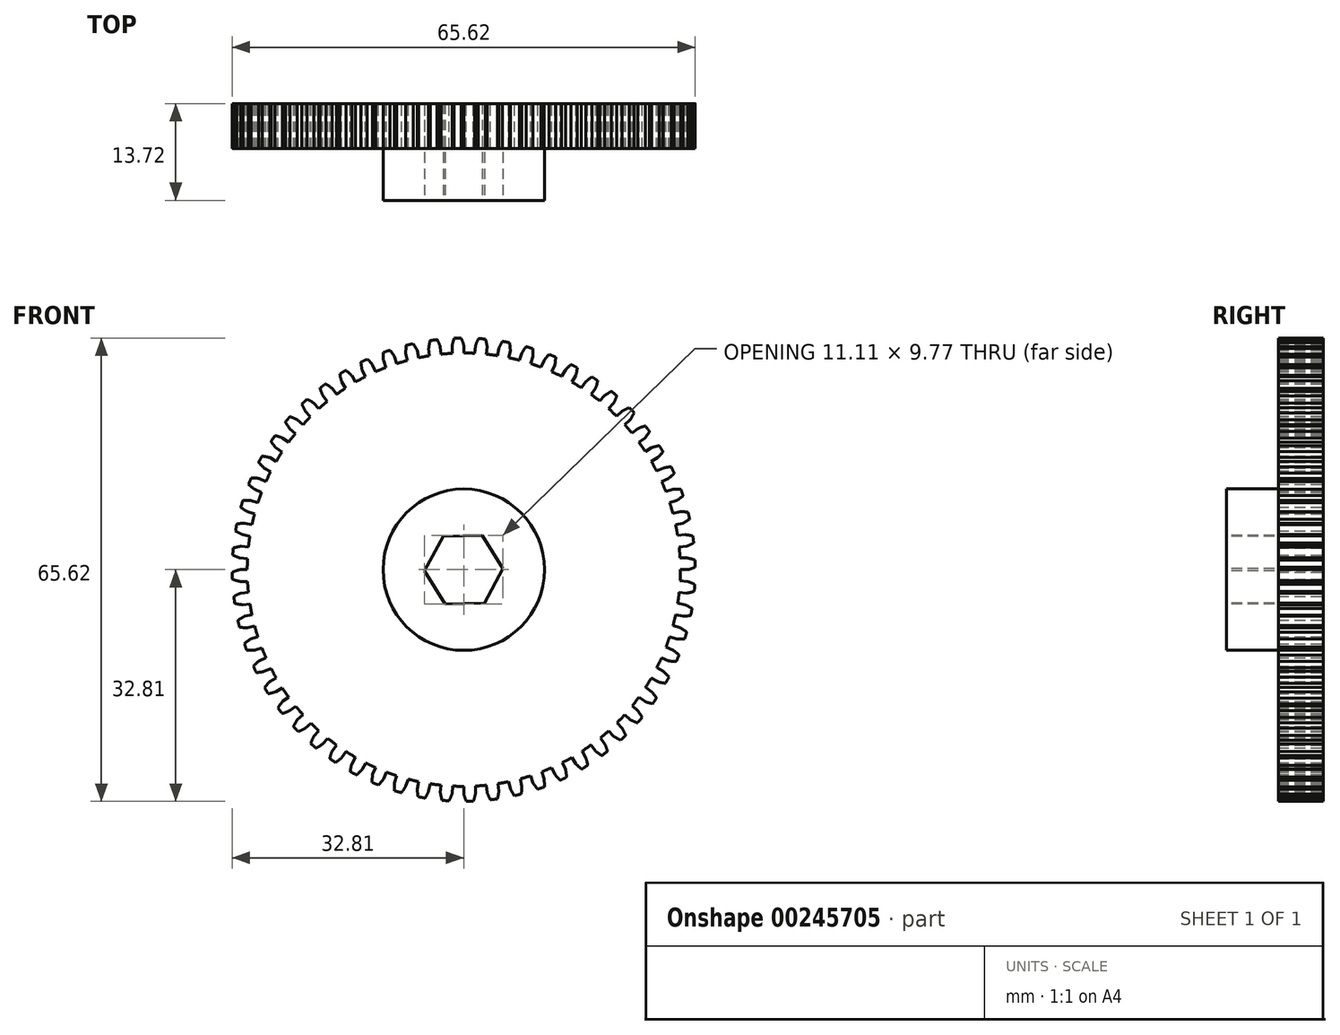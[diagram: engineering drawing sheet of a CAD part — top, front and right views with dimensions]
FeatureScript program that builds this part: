
annotation { "Feature Type Name" : "Feature", "Feature Type Description" : "" }
export const myFeature = defineFeature(function(context is Context, id is Id, definition is map)
    precondition{}
    {
        {
            var Q0;
            Q0=qCreatedBy(makeId("Front.planeOp"),FACE);
            var sketch = newSketch(context, id + "F0", { "sketchPlane" : qUnion([Q0])});
            skCircle(sketch, "E0", {"center": v(0, 0) * mm, "radius": 30.7 * mm});
            skArc(sketch, "E1", {"start": v(-0.36, 32.8) * mm, "mid": v(-0.6, 32.8) * mm, "end": v(-0.86, 32.8) * mm});
            skLineSegment(sketch, "E2", {"start": v(0, 30.7) * mm, "end": v(0, 31.75) * mm});
            skArc(sketch, "E3", {"start": v(-7.94, 31.83) * mm, "mid": v(-7.94, 31.8) * mm, "end": v(-7.94, 31.75) * mm});
            skArc(sketch, "E4.trimOffspring", {"start": v(0, 31.75) * mm, "mid": v(-0.16, 32.28) * mm, "end": v(-0.36, 32.8) * mm});
            skArc(sketch, "E5.trimOffspring", {"start": v(-7.94, 31.83) * mm, "mid": v(-8.1, 31.8) * mm, "end": v(-8.26, 31.75) * mm});
            skLineSegment(sketch, "E6.trimOffspring", {"start": v(-7.94, 31.75) * mm, "end": v(-8.26, 31.75) * mm});
            skArc(sketch, "E7.MirrorCS", {"start": v(-1.36, 32.78) * mm, "mid": v(-1.1, 32.79) * mm, "end": v(-0.86, 32.8) * mm});
            skArc(sketch, "E8.MirrorCS", {"start": v(-1.66, 31.7) * mm, "mid": v(-1.53, 32.25) * mm, "end": v(-1.36, 32.78) * mm});
            skLineSegment(sketch, "E9", {"start": v(-1.66, 31.7) * mm, "end": v(-1.66, 30.65) * mm});
            skArc(sketch, "E10.1.0", {"start": v(-3.32, 31.58) * mm, "mid": v(-3.54, 32.1) * mm, "end": v(-3.79, 32.59) * mm});
            skLineSegment(sketch, "E10.1.1", {"start": v(-3.2, 30.52) * mm, "end": v(-3.32, 31.58) * mm});
            skLineSegment(sketch, "E10.1.2", {"start": v(-4.97, 31.36) * mm, "end": v(-4.86, 30.3) * mm});
            skArc(sketch, "E10.1.3", {"start": v(-4.97, 31.36) * mm, "mid": v(-4.9, 31.91) * mm, "end": v(-4.78, 32.46) * mm});
            skArc(sketch, "E10.1.4", {"start": v(-4.78, 32.46) * mm, "mid": v(-4.53, 32.5) * mm, "end": v(-4.28, 32.53) * mm});
            skArc(sketch, "E10.1.5", {"start": v(-3.79, 32.59) * mm, "mid": v(-4.04, 32.56) * mm, "end": v(-4.28, 32.53) * mm});
            skArc(sketch, "E10.2.0", {"start": v(-6.6, 31.06) * mm, "mid": v(-6.87, 31.55) * mm, "end": v(-7.17, 32.01) * mm});
            skLineSegment(sketch, "E10.2.1", {"start": v(-6.38, 30.02) * mm, "end": v(-6.6, 31.06) * mm});
            skLineSegment(sketch, "E10.2.2", {"start": v(-8.22, 30.67) * mm, "end": v(-8, 29.63) * mm});
            skArc(sketch, "E10.2.3", {"start": v(-8.22, 30.67) * mm, "mid": v(-8.2, 31.23) * mm, "end": v(-8.14, 31.78) * mm});
            skArc(sketch, "E10.2.4", {"start": v(-8.14, 31.78) * mm, "mid": v(-7.9, 31.84) * mm, "end": v(-7.66, 31.9) * mm});
            skArc(sketch, "E10.2.5", {"start": v(-7.17, 32.01) * mm, "mid": v(-7.42, 31.96) * mm, "end": v(-7.66, 31.9) * mm});
            skArc(sketch, "E10.3.0", {"start": v(-9.81, 30.2) * mm, "mid": v(-10.13, 30.65) * mm, "end": v(-10.48, 31.09) * mm});
            skLineSegment(sketch, "E10.3.1", {"start": v(-9.48, 29.19) * mm, "end": v(-9.81, 30.2) * mm});
            skLineSegment(sketch, "E10.3.2", {"start": v(-11.38, 29.64) * mm, "end": v(-11.05, 28.63) * mm});
            skArc(sketch, "E10.3.3", {"start": v(-11.38, 29.64) * mm, "mid": v(-11.42, 30.2) * mm, "end": v(-11.42, 30.76) * mm});
            skArc(sketch, "E10.3.4", {"start": v(-11.42, 30.76) * mm, "mid": v(-11.19, 30.84) * mm, "end": v(-10.95, 30.93) * mm});
            skArc(sketch, "E10.3.5", {"start": v(-10.48, 31.09) * mm, "mid": v(-10.72, 31) * mm, "end": v(-10.95, 30.93) * mm});
            skArc(sketch, "E10.4.0", {"start": v(-12.91, 29) * mm, "mid": v(-13.28, 29.43) * mm, "end": v(-13.67, 29.82) * mm});
            skLineSegment(sketch, "E10.4.1", {"start": v(-12.48, 28.04) * mm, "end": v(-12.91, 29) * mm});
            skLineSegment(sketch, "E10.4.2", {"start": v(-14.41, 28.29) * mm, "end": v(-13.98, 27.32) * mm});
            skArc(sketch, "E10.4.3", {"start": v(-14.41, 28.29) * mm, "mid": v(-14.51, 28.84) * mm, "end": v(-14.57, 29.4) * mm});
            skArc(sketch, "E10.4.4", {"start": v(-14.57, 29.4) * mm, "mid": v(-14.35, 29.5) * mm, "end": v(-14.12, 29.61) * mm});
            skArc(sketch, "E10.4.5", {"start": v(-13.67, 29.82) * mm, "mid": v(-13.9, 29.72) * mm, "end": v(-14.12, 29.61) * mm});
            skArc(sketch, "E10.5.0", {"start": v(-15.88, 27.5) * mm, "mid": v(-16.28, 27.88) * mm, "end": v(-16.72, 28.23) * mm});
            skLineSegment(sketch, "E10.5.1", {"start": v(-15.35, 26.58) * mm, "end": v(-15.87, 27.5) * mm});
            skLineSegment(sketch, "E10.5.2", {"start": v(-17.3, 26.63) * mm, "end": v(-16.76, 25.7) * mm});
            skArc(sketch, "E10.5.3", {"start": v(-17.3, 26.63) * mm, "mid": v(-17.45, 27.16) * mm, "end": v(-17.56, 27.7) * mm});
            skArc(sketch, "E10.5.4", {"start": v(-17.56, 27.7) * mm, "mid": v(-17.35, 27.84) * mm, "end": v(-17.14, 27.97) * mm});
            skArc(sketch, "E10.5.5", {"start": v(-16.72, 28.23) * mm, "mid": v(-16.93, 28.1) * mm, "end": v(-17.14, 27.97) * mm});
            skArc(sketch, "E10.6.0", {"start": v(-18.66, 25.69) * mm, "mid": v(-19.1, 26.02) * mm, "end": v(-19.57, 26.33) * mm});
            skLineSegment(sketch, "E10.6.1", {"start": v(-18.04, 24.83) * mm, "end": v(-18.66, 25.69) * mm});
            skLineSegment(sketch, "E10.6.2", {"start": v(-19.98, 24.67) * mm, "end": v(-19.36, 23.82) * mm});
            skArc(sketch, "E10.6.3", {"start": v(-19.98, 24.67) * mm, "mid": v(-20.2, 25.2) * mm, "end": v(-20.36, 25.72) * mm});
            skArc(sketch, "E10.6.4", {"start": v(-20.36, 25.72) * mm, "mid": v(-20.17, 25.88) * mm, "end": v(-19.97, 26.03) * mm});
            skArc(sketch, "E10.6.5", {"start": v(-19.57, 26.33) * mm, "mid": v(-19.77, 26.18) * mm, "end": v(-19.97, 26.03) * mm});
            skArc(sketch, "E10.7.0", {"start": v(-21.24, 23.6) * mm, "mid": v(-21.72, 23.88) * mm, "end": v(-22.22, 24.14) * mm});
            skLineSegment(sketch, "E10.7.1", {"start": v(-20.54, 22.8) * mm, "end": v(-21.24, 23.6) * mm});
            skLineSegment(sketch, "E10.7.2", {"start": v(-22.45, 22.45) * mm, "end": v(-21.74, 21.66) * mm});
            skArc(sketch, "E10.7.3", {"start": v(-22.45, 22.45) * mm, "mid": v(-22.71, 22.94) * mm, "end": v(-22.94, 23.45) * mm});
            skArc(sketch, "E10.7.4", {"start": v(-22.94, 23.45) * mm, "mid": v(-22.76, 23.63) * mm, "end": v(-22.58, 23.8) * mm});
            skArc(sketch, "E10.7.5", {"start": v(-22.22, 24.14) * mm, "mid": v(-22.4, 23.97) * mm, "end": v(-22.58, 23.8) * mm});
            skArc(sketch, "E10.8.0", {"start": v(-23.6, 21.24) * mm, "mid": v(-24.1, 21.48) * mm, "end": v(-24.62, 21.68) * mm});
            skLineSegment(sketch, "E10.8.1", {"start": v(-22.8, 20.54) * mm, "end": v(-23.6, 21.24) * mm});
            skLineSegment(sketch, "E10.8.2", {"start": v(-24.67, 19.98) * mm, "end": v(-23.89, 19.27) * mm});
            skArc(sketch, "E10.8.3", {"start": v(-24.67, 19.98) * mm, "mid": v(-24.99, 20.44) * mm, "end": v(-25.27, 20.93) * mm});
            skArc(sketch, "E10.8.4", {"start": v(-25.27, 20.93) * mm, "mid": v(-25.1, 21.12) * mm, "end": v(-24.95, 21.3) * mm});
            skArc(sketch, "E10.8.5", {"start": v(-24.62, 21.68) * mm, "mid": v(-24.78, 21.5) * mm, "end": v(-24.95, 21.3) * mm});
            skArc(sketch, "E10.9.0", {"start": v(-25.69, 18.66) * mm, "mid": v(-26.21, 18.85) * mm, "end": v(-26.75, 19) * mm});
            skLineSegment(sketch, "E10.9.1", {"start": v(-24.83, 18.04) * mm, "end": v(-25.69, 18.66) * mm});
            skLineSegment(sketch, "E10.9.2", {"start": v(-26.63, 17.3) * mm, "end": v(-25.77, 16.67) * mm});
            skArc(sketch, "E10.9.3", {"start": v(-26.63, 17.3) * mm, "mid": v(-26.99, 17.72) * mm, "end": v(-27.32, 18.17) * mm});
            skArc(sketch, "E10.9.4", {"start": v(-27.32, 18.17) * mm, "mid": v(-27.18, 18.38) * mm, "end": v(-27.04, 18.58) * mm});
            skArc(sketch, "E10.9.5", {"start": v(-26.75, 19) * mm, "mid": v(-26.9, 18.79) * mm, "end": v(-27.04, 18.58) * mm});
            skArc(sketch, "E10.10.0", {"start": v(-27.5, 15.88) * mm, "mid": v(-28.04, 16) * mm, "end": v(-28.6, 16.1) * mm});
            skLineSegment(sketch, "E10.10.1", {"start": v(-26.58, 15.35) * mm, "end": v(-27.5, 15.88) * mm});
            skLineSegment(sketch, "E10.10.2", {"start": v(-28.29, 14.41) * mm, "end": v(-27.37, 13.88) * mm});
            skArc(sketch, "E10.10.3", {"start": v(-28.29, 14.41) * mm, "mid": v(-28.7, 14.8) * mm, "end": v(-29.07, 15.22) * mm});
            skArc(sketch, "E10.10.4", {"start": v(-29.07, 15.22) * mm, "mid": v(-28.95, 15.44) * mm, "end": v(-28.83, 15.65) * mm});
            skArc(sketch, "E10.10.5", {"start": v(-28.6, 16.1) * mm, "mid": v(-28.71, 15.87) * mm, "end": v(-28.83, 15.65) * mm});
            skArc(sketch, "E10.11.0", {"start": v(-29, 12.91) * mm, "mid": v(-29.56, 12.98) * mm, "end": v(-30.12, 13.01) * mm});
            skLineSegment(sketch, "E10.11.1", {"start": v(-28.04, 12.48) * mm, "end": v(-29, 12.91) * mm});
            skLineSegment(sketch, "E10.11.2", {"start": v(-29.64, 11.38) * mm, "end": v(-28.67, 10.95) * mm});
            skArc(sketch, "E10.11.3", {"start": v(-29.64, 11.38) * mm, "mid": v(-30.08, 11.72) * mm, "end": v(-30.5, 12.1) * mm});
            skArc(sketch, "E10.11.4", {"start": v(-30.5, 12.1) * mm, "mid": v(-30.4, 12.32) * mm, "end": v(-30.31, 12.56) * mm});
            skArc(sketch, "E10.11.5", {"start": v(-30.12, 13.01) * mm, "mid": v(-30.21, 12.78) * mm, "end": v(-30.31, 12.56) * mm});
            skArc(sketch, "E10.12.0", {"start": v(-30.2, 9.81) * mm, "mid": v(-30.75, 9.82) * mm, "end": v(-31.31, 9.8) * mm});
            skLineSegment(sketch, "E10.12.1", {"start": v(-29.19, 9.48) * mm, "end": v(-30.2, 9.81) * mm});
            skLineSegment(sketch, "E10.12.2", {"start": v(-30.67, 8.22) * mm, "end": v(-29.66, 7.89) * mm});
            skArc(sketch, "E10.12.3", {"start": v(-30.67, 8.22) * mm, "mid": v(-31.14, 8.51) * mm, "end": v(-31.6, 8.84) * mm});
            skArc(sketch, "E10.12.4", {"start": v(-31.6, 8.84) * mm, "mid": v(-31.53, 9.08) * mm, "end": v(-31.46, 9.32) * mm});
            skArc(sketch, "E10.12.5", {"start": v(-31.31, 9.8) * mm, "mid": v(-31.39, 9.56) * mm, "end": v(-31.46, 9.32) * mm});
            skArc(sketch, "E10.13.0", {"start": v(-31.06, 6.6) * mm, "mid": v(-31.61, 6.55) * mm, "end": v(-32.16, 6.47) * mm});
            skLineSegment(sketch, "E10.13.1", {"start": v(-30.02, 6.38) * mm, "end": v(-31.06, 6.6) * mm});
            skLineSegment(sketch, "E10.13.2", {"start": v(-31.36, 4.97) * mm, "end": v(-30.32, 4.75) * mm});
            skArc(sketch, "E10.13.3", {"start": v(-31.36, 4.97) * mm, "mid": v(-31.86, 5.21) * mm, "end": v(-32.35, 5.49) * mm});
            skArc(sketch, "E10.13.4", {"start": v(-32.35, 5.49) * mm, "mid": v(-32.3, 5.73) * mm, "end": v(-32.26, 5.98) * mm});
            skArc(sketch, "E10.13.5", {"start": v(-32.16, 6.47) * mm, "mid": v(-32.21, 6.22) * mm, "end": v(-32.26, 5.98) * mm});
            skArc(sketch, "E10.14.0", {"start": v(-31.58, 3.32) * mm, "mid": v(-32.12, 3.21) * mm, "end": v(-32.66, 3.07) * mm});
            skLineSegment(sketch, "E10.14.1", {"start": v(-30.52, 3.2) * mm, "end": v(-31.58, 3.32) * mm});
            skLineSegment(sketch, "E10.14.2", {"start": v(-31.7, 1.66) * mm, "end": v(-30.65, 1.55) * mm});
            skArc(sketch, "E10.14.3", {"start": v(-31.7, 1.66) * mm, "mid": v(-32.23, 1.85) * mm, "end": v(-32.74, 2.08) * mm});
            skArc(sketch, "E10.14.4", {"start": v(-32.74, 2.08) * mm, "mid": v(-32.73, 2.33) * mm, "end": v(-32.7, 2.57) * mm});
            skArc(sketch, "E10.14.5", {"start": v(-32.66, 3.07) * mm, "mid": v(-32.69, 2.82) * mm, "end": v(-32.7, 2.57) * mm});
            skArc(sketch, "E10.15.0", {"start": v(-31.75, 0) * mm, "mid": v(-32.28, -0.16) * mm, "end": v(-32.8, -0.36) * mm});
            skLineSegment(sketch, "E10.15.1", {"start": v(-30.7, 0) * mm, "end": v(-31.75, 0) * mm});
            skLineSegment(sketch, "E10.15.2", {"start": v(-31.7, -1.66) * mm, "end": v(-30.65, -1.66) * mm});
            skArc(sketch, "E10.15.3", {"start": v(-31.7, -1.66) * mm, "mid": v(-32.25, -1.53) * mm, "end": v(-32.78, -1.36) * mm});
            skArc(sketch, "E10.15.4", {"start": v(-32.78, -1.36) * mm, "mid": v(-32.79, -1.1) * mm, "end": v(-32.8, -0.86) * mm});
            skArc(sketch, "E10.15.5", {"start": v(-32.8, -0.36) * mm, "mid": v(-32.8, -0.6) * mm, "end": v(-32.8, -0.86) * mm});
            skArc(sketch, "E10.16.0", {"start": v(-31.58, -3.32) * mm, "mid": v(-32.1, -3.54) * mm, "end": v(-32.59, -3.79) * mm});
            skLineSegment(sketch, "E10.16.1", {"start": v(-30.52, -3.2) * mm, "end": v(-31.58, -3.32) * mm});
            skLineSegment(sketch, "E10.16.2", {"start": v(-31.36, -4.97) * mm, "end": v(-30.3, -4.86) * mm});
            skArc(sketch, "E10.16.3", {"start": v(-31.36, -4.97) * mm, "mid": v(-31.91, -4.9) * mm, "end": v(-32.46, -4.78) * mm});
            skArc(sketch, "E10.16.4", {"start": v(-32.46, -4.78) * mm, "mid": v(-32.5, -4.53) * mm, "end": v(-32.53, -4.28) * mm});
            skArc(sketch, "E10.16.5", {"start": v(-32.59, -3.79) * mm, "mid": v(-32.56, -4.04) * mm, "end": v(-32.53, -4.28) * mm});
            skArc(sketch, "E10.17.0", {"start": v(-31.06, -6.6) * mm, "mid": v(-31.55, -6.87) * mm, "end": v(-32.01, -7.17) * mm});
            skLineSegment(sketch, "E10.17.1", {"start": v(-30.02, -6.38) * mm, "end": v(-31.06, -6.6) * mm});
            skLineSegment(sketch, "E10.17.2", {"start": v(-30.67, -8.22) * mm, "end": v(-29.63, -8) * mm});
            skArc(sketch, "E10.17.3", {"start": v(-30.67, -8.22) * mm, "mid": v(-31.23, -8.2) * mm, "end": v(-31.78, -8.14) * mm});
            skArc(sketch, "E10.17.4", {"start": v(-31.78, -8.14) * mm, "mid": v(-31.84, -7.9) * mm, "end": v(-31.9, -7.66) * mm});
            skArc(sketch, "E10.17.5", {"start": v(-32.01, -7.17) * mm, "mid": v(-31.96, -7.42) * mm, "end": v(-31.9, -7.66) * mm});
            skArc(sketch, "E10.18.0", {"start": v(-30.2, -9.81) * mm, "mid": v(-30.65, -10.13) * mm, "end": v(-31.09, -10.48) * mm});
            skLineSegment(sketch, "E10.18.1", {"start": v(-29.19, -9.48) * mm, "end": v(-30.2, -9.81) * mm});
            skLineSegment(sketch, "E10.18.2", {"start": v(-29.64, -11.38) * mm, "end": v(-28.63, -11.05) * mm});
            skArc(sketch, "E10.18.3", {"start": v(-29.64, -11.38) * mm, "mid": v(-30.2, -11.42) * mm, "end": v(-30.76, -11.42) * mm});
            skArc(sketch, "E10.18.4", {"start": v(-30.76, -11.42) * mm, "mid": v(-30.84, -11.19) * mm, "end": v(-30.93, -10.95) * mm});
            skArc(sketch, "E10.18.5", {"start": v(-31.09, -10.48) * mm, "mid": v(-31, -10.72) * mm, "end": v(-30.93, -10.95) * mm});
            skArc(sketch, "E10.19.0", {"start": v(-29, -12.91) * mm, "mid": v(-29.43, -13.28) * mm, "end": v(-29.82, -13.67) * mm});
            skLineSegment(sketch, "E10.19.1", {"start": v(-28.04, -12.48) * mm, "end": v(-29, -12.91) * mm});
            skLineSegment(sketch, "E10.19.2", {"start": v(-28.29, -14.41) * mm, "end": v(-27.32, -13.98) * mm});
            skArc(sketch, "E10.19.3", {"start": v(-28.29, -14.41) * mm, "mid": v(-28.84, -14.51) * mm, "end": v(-29.4, -14.57) * mm});
            skArc(sketch, "E10.19.4", {"start": v(-29.4, -14.57) * mm, "mid": v(-29.5, -14.35) * mm, "end": v(-29.61, -14.12) * mm});
            skArc(sketch, "E10.19.5", {"start": v(-29.82, -13.67) * mm, "mid": v(-29.72, -13.9) * mm, "end": v(-29.61, -14.12) * mm});
            skArc(sketch, "E10.20.0", {"start": v(-27.5, -15.87) * mm, "mid": v(-27.88, -16.28) * mm, "end": v(-28.23, -16.72) * mm});
            skLineSegment(sketch, "E10.20.1", {"start": v(-26.58, -15.35) * mm, "end": v(-27.5, -15.87) * mm});
            skLineSegment(sketch, "E10.20.2", {"start": v(-26.63, -17.3) * mm, "end": v(-25.7, -16.76) * mm});
            skArc(sketch, "E10.20.3", {"start": v(-26.63, -17.3) * mm, "mid": v(-27.16, -17.45) * mm, "end": v(-27.7, -17.56) * mm});
            skArc(sketch, "E10.20.4", {"start": v(-27.7, -17.56) * mm, "mid": v(-27.84, -17.35) * mm, "end": v(-27.97, -17.14) * mm});
            skArc(sketch, "E10.20.5", {"start": v(-28.23, -16.72) * mm, "mid": v(-28.1, -16.93) * mm, "end": v(-27.97, -17.14) * mm});
            skArc(sketch, "E10.21.0", {"start": v(-25.69, -18.66) * mm, "mid": v(-26.02, -19.1) * mm, "end": v(-26.33, -19.57) * mm});
            skLineSegment(sketch, "E10.21.1", {"start": v(-24.83, -18.04) * mm, "end": v(-25.69, -18.66) * mm});
            skLineSegment(sketch, "E10.21.2", {"start": v(-24.67, -19.98) * mm, "end": v(-23.82, -19.36) * mm});
            skArc(sketch, "E10.21.3", {"start": v(-24.67, -19.98) * mm, "mid": v(-25.2, -20.2) * mm, "end": v(-25.72, -20.36) * mm});
            skArc(sketch, "E10.21.4", {"start": v(-25.72, -20.36) * mm, "mid": v(-25.88, -20.17) * mm, "end": v(-26.03, -19.97) * mm});
            skArc(sketch, "E10.21.5", {"start": v(-26.33, -19.57) * mm, "mid": v(-26.18, -19.77) * mm, "end": v(-26.03, -19.97) * mm});
            skArc(sketch, "E10.22.0", {"start": v(-23.6, -21.24) * mm, "mid": v(-23.88, -21.72) * mm, "end": v(-24.14, -22.22) * mm});
            skLineSegment(sketch, "E10.22.1", {"start": v(-22.8, -20.54) * mm, "end": v(-23.6, -21.24) * mm});
            skLineSegment(sketch, "E10.22.2", {"start": v(-22.45, -22.45) * mm, "end": v(-21.66, -21.74) * mm});
            skArc(sketch, "E10.22.3", {"start": v(-22.45, -22.45) * mm, "mid": v(-22.94, -22.71) * mm, "end": v(-23.45, -22.94) * mm});
            skArc(sketch, "E10.22.4", {"start": v(-23.45, -22.94) * mm, "mid": v(-23.63, -22.76) * mm, "end": v(-23.8, -22.58) * mm});
            skArc(sketch, "E10.22.5", {"start": v(-24.14, -22.22) * mm, "mid": v(-23.97, -22.4) * mm, "end": v(-23.8, -22.58) * mm});
            skArc(sketch, "E10.23.0", {"start": v(-21.24, -23.6) * mm, "mid": v(-21.48, -24.1) * mm, "end": v(-21.68, -24.62) * mm});
            skLineSegment(sketch, "E10.23.1", {"start": v(-20.54, -22.8) * mm, "end": v(-21.24, -23.6) * mm});
            skLineSegment(sketch, "E10.23.2", {"start": v(-19.98, -24.67) * mm, "end": v(-19.27, -23.89) * mm});
            skArc(sketch, "E10.23.3", {"start": v(-19.98, -24.67) * mm, "mid": v(-20.44, -24.99) * mm, "end": v(-20.93, -25.27) * mm});
            skArc(sketch, "E10.23.4", {"start": v(-20.93, -25.27) * mm, "mid": v(-21.12, -25.1) * mm, "end": v(-21.3, -24.95) * mm});
            skArc(sketch, "E10.23.5", {"start": v(-21.68, -24.62) * mm, "mid": v(-21.5, -24.78) * mm, "end": v(-21.3, -24.95) * mm});
            skArc(sketch, "E10.24.0", {"start": v(-18.66, -25.69) * mm, "mid": v(-18.85, -26.21) * mm, "end": v(-19, -26.75) * mm});
            skLineSegment(sketch, "E10.24.1", {"start": v(-18.04, -24.83) * mm, "end": v(-18.66, -25.69) * mm});
            skLineSegment(sketch, "E10.24.2", {"start": v(-17.3, -26.63) * mm, "end": v(-16.67, -25.77) * mm});
            skArc(sketch, "E10.24.3", {"start": v(-17.3, -26.63) * mm, "mid": v(-17.72, -26.99) * mm, "end": v(-18.17, -27.32) * mm});
            skArc(sketch, "E10.24.4", {"start": v(-18.17, -27.32) * mm, "mid": v(-18.38, -27.18) * mm, "end": v(-18.58, -27.04) * mm});
            skArc(sketch, "E10.24.5", {"start": v(-19, -26.75) * mm, "mid": v(-18.79, -26.9) * mm, "end": v(-18.58, -27.04) * mm});
            skArc(sketch, "E10.25.0", {"start": v(-15.87, -27.5) * mm, "mid": v(-16, -28.04) * mm, "end": v(-16.1, -28.6) * mm});
            skLineSegment(sketch, "E10.25.1", {"start": v(-15.35, -26.58) * mm, "end": v(-15.87, -27.5) * mm});
            skLineSegment(sketch, "E10.25.2", {"start": v(-14.41, -28.29) * mm, "end": v(-13.88, -27.37) * mm});
            skArc(sketch, "E10.25.3", {"start": v(-14.41, -28.29) * mm, "mid": v(-14.8, -28.7) * mm, "end": v(-15.22, -29.07) * mm});
            skArc(sketch, "E10.25.4", {"start": v(-15.22, -29.07) * mm, "mid": v(-15.44, -28.95) * mm, "end": v(-15.65, -28.83) * mm});
            skArc(sketch, "E10.25.5", {"start": v(-16.1, -28.6) * mm, "mid": v(-15.87, -28.71) * mm, "end": v(-15.65, -28.83) * mm});
            skArc(sketch, "E10.26.0", {"start": v(-12.91, -29) * mm, "mid": v(-12.98, -29.56) * mm, "end": v(-13.01, -30.12) * mm});
            skLineSegment(sketch, "E10.26.1", {"start": v(-12.48, -28.04) * mm, "end": v(-12.91, -29) * mm});
            skLineSegment(sketch, "E10.26.2", {"start": v(-11.38, -29.64) * mm, "end": v(-10.95, -28.67) * mm});
            skArc(sketch, "E10.26.3", {"start": v(-11.38, -29.64) * mm, "mid": v(-11.72, -30.08) * mm, "end": v(-12.1, -30.5) * mm});
            skArc(sketch, "E10.26.4", {"start": v(-12.1, -30.5) * mm, "mid": v(-12.32, -30.4) * mm, "end": v(-12.56, -30.31) * mm});
            skArc(sketch, "E10.26.5", {"start": v(-13.01, -30.12) * mm, "mid": v(-12.78, -30.21) * mm, "end": v(-12.56, -30.31) * mm});
            skArc(sketch, "E10.27.0", {"start": v(-9.81, -30.2) * mm, "mid": v(-9.82, -30.75) * mm, "end": v(-9.8, -31.31) * mm});
            skLineSegment(sketch, "E10.27.1", {"start": v(-9.48, -29.19) * mm, "end": v(-9.81, -30.2) * mm});
            skLineSegment(sketch, "E10.27.2", {"start": v(-8.22, -30.67) * mm, "end": v(-7.89, -29.66) * mm});
            skArc(sketch, "E10.27.3", {"start": v(-8.22, -30.67) * mm, "mid": v(-8.51, -31.14) * mm, "end": v(-8.84, -31.6) * mm});
            skArc(sketch, "E10.27.4", {"start": v(-8.84, -31.6) * mm, "mid": v(-9.08, -31.53) * mm, "end": v(-9.32, -31.46) * mm});
            skArc(sketch, "E10.27.5", {"start": v(-9.8, -31.31) * mm, "mid": v(-9.56, -31.39) * mm, "end": v(-9.32, -31.46) * mm});
            skArc(sketch, "E10.28.0", {"start": v(-6.6, -31.06) * mm, "mid": v(-6.55, -31.61) * mm, "end": v(-6.47, -32.16) * mm});
            skLineSegment(sketch, "E10.28.1", {"start": v(-6.38, -30.02) * mm, "end": v(-6.6, -31.06) * mm});
            skLineSegment(sketch, "E10.28.2", {"start": v(-4.97, -31.36) * mm, "end": v(-4.75, -30.32) * mm});
            skArc(sketch, "E10.28.3", {"start": v(-4.97, -31.36) * mm, "mid": v(-5.21, -31.86) * mm, "end": v(-5.49, -32.35) * mm});
            skArc(sketch, "E10.28.4", {"start": v(-5.49, -32.35) * mm, "mid": v(-5.73, -32.3) * mm, "end": v(-5.98, -32.26) * mm});
            skArc(sketch, "E10.28.5", {"start": v(-6.47, -32.16) * mm, "mid": v(-6.22, -32.21) * mm, "end": v(-5.98, -32.26) * mm});
            skArc(sketch, "E10.29.0", {"start": v(-3.32, -31.58) * mm, "mid": v(-3.21, -32.12) * mm, "end": v(-3.07, -32.66) * mm});
            skLineSegment(sketch, "E10.29.1", {"start": v(-3.2, -30.52) * mm, "end": v(-3.32, -31.58) * mm});
            skLineSegment(sketch, "E10.29.2", {"start": v(-1.66, -31.7) * mm, "end": v(-1.55, -30.65) * mm});
            skArc(sketch, "E10.29.3", {"start": v(-1.66, -31.7) * mm, "mid": v(-1.85, -32.23) * mm, "end": v(-2.08, -32.74) * mm});
            skArc(sketch, "E10.29.4", {"start": v(-2.08, -32.74) * mm, "mid": v(-2.33, -32.73) * mm, "end": v(-2.57, -32.7) * mm});
            skArc(sketch, "E10.29.5", {"start": v(-3.07, -32.66) * mm, "mid": v(-2.82, -32.69) * mm, "end": v(-2.57, -32.7) * mm});
            skArc(sketch, "E10.30.0", {"start": v(0, -31.75) * mm, "mid": v(0.16, -32.28) * mm, "end": v(0.36, -32.8) * mm});
            skLineSegment(sketch, "E10.30.1", {"start": v(0, -30.7) * mm, "end": v(0, -31.75) * mm});
            skLineSegment(sketch, "E10.30.2", {"start": v(1.66, -31.7) * mm, "end": v(1.66, -30.65) * mm});
            skArc(sketch, "E10.30.3", {"start": v(1.66, -31.7) * mm, "mid": v(1.53, -32.25) * mm, "end": v(1.36, -32.78) * mm});
            skArc(sketch, "E10.30.4", {"start": v(1.36, -32.78) * mm, "mid": v(1.1, -32.79) * mm, "end": v(0.86, -32.8) * mm});
            skArc(sketch, "E10.30.5", {"start": v(0.36, -32.8) * mm, "mid": v(0.6, -32.8) * mm, "end": v(0.86, -32.8) * mm});
            skArc(sketch, "E10.31.0", {"start": v(3.32, -31.58) * mm, "mid": v(3.54, -32.1) * mm, "end": v(3.79, -32.59) * mm});
            skLineSegment(sketch, "E10.31.1", {"start": v(3.2, -30.52) * mm, "end": v(3.32, -31.58) * mm});
            skLineSegment(sketch, "E10.31.2", {"start": v(4.97, -31.36) * mm, "end": v(4.86, -30.3) * mm});
            skArc(sketch, "E10.31.3", {"start": v(4.97, -31.36) * mm, "mid": v(4.9, -31.91) * mm, "end": v(4.78, -32.46) * mm});
            skArc(sketch, "E10.31.4", {"start": v(4.78, -32.46) * mm, "mid": v(4.53, -32.5) * mm, "end": v(4.28, -32.53) * mm});
            skArc(sketch, "E10.31.5", {"start": v(3.79, -32.59) * mm, "mid": v(4.04, -32.56) * mm, "end": v(4.28, -32.53) * mm});
            skArc(sketch, "E10.32.0", {"start": v(6.6, -31.06) * mm, "mid": v(6.87, -31.55) * mm, "end": v(7.17, -32.01) * mm});
            skLineSegment(sketch, "E10.32.1", {"start": v(6.38, -30.02) * mm, "end": v(6.6, -31.06) * mm});
            skLineSegment(sketch, "E10.32.2", {"start": v(8.22, -30.67) * mm, "end": v(8, -29.63) * mm});
            skArc(sketch, "E10.32.3", {"start": v(8.22, -30.67) * mm, "mid": v(8.2, -31.23) * mm, "end": v(8.14, -31.78) * mm});
            skArc(sketch, "E10.32.4", {"start": v(8.14, -31.78) * mm, "mid": v(7.9, -31.84) * mm, "end": v(7.66, -31.9) * mm});
            skArc(sketch, "E10.32.5", {"start": v(7.17, -32.01) * mm, "mid": v(7.42, -31.96) * mm, "end": v(7.66, -31.9) * mm});
            skArc(sketch, "E10.33.0", {"start": v(9.81, -30.2) * mm, "mid": v(10.13, -30.65) * mm, "end": v(10.48, -31.09) * mm});
            skLineSegment(sketch, "E10.33.1", {"start": v(9.48, -29.19) * mm, "end": v(9.81, -30.2) * mm});
            skLineSegment(sketch, "E10.33.2", {"start": v(11.38, -29.64) * mm, "end": v(11.05, -28.63) * mm});
            skArc(sketch, "E10.33.3", {"start": v(11.38, -29.64) * mm, "mid": v(11.42, -30.2) * mm, "end": v(11.42, -30.76) * mm});
            skArc(sketch, "E10.33.4", {"start": v(11.42, -30.76) * mm, "mid": v(11.19, -30.84) * mm, "end": v(10.95, -30.93) * mm});
            skArc(sketch, "E10.33.5", {"start": v(10.48, -31.09) * mm, "mid": v(10.72, -31) * mm, "end": v(10.95, -30.93) * mm});
            skArc(sketch, "E10.34.0", {"start": v(12.91, -29) * mm, "mid": v(13.28, -29.43) * mm, "end": v(13.67, -29.82) * mm});
            skLineSegment(sketch, "E10.34.1", {"start": v(12.48, -28.04) * mm, "end": v(12.91, -29) * mm});
            skLineSegment(sketch, "E10.34.2", {"start": v(14.41, -28.29) * mm, "end": v(13.98, -27.32) * mm});
            skArc(sketch, "E10.34.3", {"start": v(14.41, -28.29) * mm, "mid": v(14.51, -28.84) * mm, "end": v(14.57, -29.4) * mm});
            skArc(sketch, "E10.34.4", {"start": v(14.57, -29.4) * mm, "mid": v(14.35, -29.5) * mm, "end": v(14.12, -29.61) * mm});
            skArc(sketch, "E10.34.5", {"start": v(13.67, -29.82) * mm, "mid": v(13.9, -29.72) * mm, "end": v(14.12, -29.61) * mm});
            skArc(sketch, "E10.35.0", {"start": v(15.87, -27.5) * mm, "mid": v(16.28, -27.88) * mm, "end": v(16.72, -28.23) * mm});
            skLineSegment(sketch, "E10.35.1", {"start": v(15.35, -26.58) * mm, "end": v(15.87, -27.5) * mm});
            skLineSegment(sketch, "E10.35.2", {"start": v(17.3, -26.63) * mm, "end": v(16.76, -25.7) * mm});
            skArc(sketch, "E10.35.3", {"start": v(17.3, -26.63) * mm, "mid": v(17.45, -27.16) * mm, "end": v(17.56, -27.7) * mm});
            skArc(sketch, "E10.35.4", {"start": v(17.56, -27.7) * mm, "mid": v(17.35, -27.84) * mm, "end": v(17.14, -27.97) * mm});
            skArc(sketch, "E10.35.5", {"start": v(16.72, -28.23) * mm, "mid": v(16.93, -28.1) * mm, "end": v(17.14, -27.97) * mm});
            skArc(sketch, "E10.36.0", {"start": v(18.66, -25.69) * mm, "mid": v(19.1, -26.02) * mm, "end": v(19.57, -26.33) * mm});
            skLineSegment(sketch, "E10.36.1", {"start": v(18.04, -24.83) * mm, "end": v(18.66, -25.69) * mm});
            skLineSegment(sketch, "E10.36.2", {"start": v(19.98, -24.67) * mm, "end": v(19.36, -23.82) * mm});
            skArc(sketch, "E10.36.3", {"start": v(19.98, -24.67) * mm, "mid": v(20.2, -25.2) * mm, "end": v(20.36, -25.72) * mm});
            skArc(sketch, "E10.36.4", {"start": v(20.36, -25.72) * mm, "mid": v(20.17, -25.88) * mm, "end": v(19.97, -26.03) * mm});
            skArc(sketch, "E10.36.5", {"start": v(19.57, -26.33) * mm, "mid": v(19.77, -26.18) * mm, "end": v(19.97, -26.03) * mm});
            skArc(sketch, "E10.37.0", {"start": v(21.24, -23.6) * mm, "mid": v(21.72, -23.88) * mm, "end": v(22.22, -24.14) * mm});
            skLineSegment(sketch, "E10.37.1", {"start": v(20.54, -22.8) * mm, "end": v(21.24, -23.6) * mm});
            skLineSegment(sketch, "E10.37.2", {"start": v(22.45, -22.45) * mm, "end": v(21.74, -21.66) * mm});
            skArc(sketch, "E10.37.3", {"start": v(22.45, -22.45) * mm, "mid": v(22.71, -22.94) * mm, "end": v(22.94, -23.45) * mm});
            skArc(sketch, "E10.37.4", {"start": v(22.94, -23.45) * mm, "mid": v(22.76, -23.63) * mm, "end": v(22.58, -23.8) * mm});
            skArc(sketch, "E10.37.5", {"start": v(22.22, -24.14) * mm, "mid": v(22.4, -23.97) * mm, "end": v(22.58, -23.8) * mm});
            skArc(sketch, "E10.38.0", {"start": v(23.6, -21.24) * mm, "mid": v(24.1, -21.48) * mm, "end": v(24.62, -21.68) * mm});
            skLineSegment(sketch, "E10.38.1", {"start": v(22.8, -20.54) * mm, "end": v(23.6, -21.24) * mm});
            skLineSegment(sketch, "E10.38.2", {"start": v(24.67, -19.98) * mm, "end": v(23.89, -19.27) * mm});
            skArc(sketch, "E10.38.3", {"start": v(24.67, -19.98) * mm, "mid": v(24.99, -20.44) * mm, "end": v(25.27, -20.93) * mm});
            skArc(sketch, "E10.38.4", {"start": v(25.27, -20.93) * mm, "mid": v(25.1, -21.12) * mm, "end": v(24.95, -21.3) * mm});
            skArc(sketch, "E10.38.5", {"start": v(24.62, -21.68) * mm, "mid": v(24.78, -21.5) * mm, "end": v(24.95, -21.3) * mm});
            skArc(sketch, "E10.39.0", {"start": v(25.69, -18.66) * mm, "mid": v(26.21, -18.85) * mm, "end": v(26.75, -19) * mm});
            skLineSegment(sketch, "E10.39.1", {"start": v(24.83, -18.04) * mm, "end": v(25.69, -18.66) * mm});
            skLineSegment(sketch, "E10.39.2", {"start": v(26.63, -17.3) * mm, "end": v(25.77, -16.67) * mm});
            skArc(sketch, "E10.39.3", {"start": v(26.63, -17.3) * mm, "mid": v(26.99, -17.72) * mm, "end": v(27.32, -18.17) * mm});
            skArc(sketch, "E10.39.4", {"start": v(27.32, -18.17) * mm, "mid": v(27.18, -18.38) * mm, "end": v(27.04, -18.58) * mm});
            skArc(sketch, "E10.39.5", {"start": v(26.75, -19) * mm, "mid": v(26.9, -18.79) * mm, "end": v(27.04, -18.58) * mm});
            skArc(sketch, "E10.40.0", {"start": v(27.5, -15.88) * mm, "mid": v(28.04, -16) * mm, "end": v(28.6, -16.1) * mm});
            skLineSegment(sketch, "E10.40.1", {"start": v(26.58, -15.35) * mm, "end": v(27.5, -15.88) * mm});
            skLineSegment(sketch, "E10.40.2", {"start": v(28.29, -14.41) * mm, "end": v(27.37, -13.88) * mm});
            skArc(sketch, "E10.40.3", {"start": v(28.29, -14.41) * mm, "mid": v(28.7, -14.8) * mm, "end": v(29.07, -15.22) * mm});
            skArc(sketch, "E10.40.4", {"start": v(29.07, -15.22) * mm, "mid": v(28.95, -15.44) * mm, "end": v(28.83, -15.65) * mm});
            skArc(sketch, "E10.40.5", {"start": v(28.6, -16.1) * mm, "mid": v(28.71, -15.87) * mm, "end": v(28.83, -15.65) * mm});
            skArc(sketch, "E10.41.0", {"start": v(29, -12.91) * mm, "mid": v(29.56, -12.98) * mm, "end": v(30.12, -13.01) * mm});
            skLineSegment(sketch, "E10.41.1", {"start": v(28.04, -12.48) * mm, "end": v(29, -12.91) * mm});
            skLineSegment(sketch, "E10.41.2", {"start": v(29.64, -11.38) * mm, "end": v(28.67, -10.95) * mm});
            skArc(sketch, "E10.41.3", {"start": v(29.64, -11.38) * mm, "mid": v(30.08, -11.72) * mm, "end": v(30.5, -12.1) * mm});
            skArc(sketch, "E10.41.4", {"start": v(30.5, -12.1) * mm, "mid": v(30.4, -12.32) * mm, "end": v(30.31, -12.56) * mm});
            skArc(sketch, "E10.41.5", {"start": v(30.12, -13.01) * mm, "mid": v(30.21, -12.78) * mm, "end": v(30.31, -12.56) * mm});
            skArc(sketch, "E10.42.0", {"start": v(30.2, -9.81) * mm, "mid": v(30.75, -9.82) * mm, "end": v(31.31, -9.8) * mm});
            skLineSegment(sketch, "E10.42.1", {"start": v(29.19, -9.48) * mm, "end": v(30.2, -9.81) * mm});
            skLineSegment(sketch, "E10.42.2", {"start": v(30.67, -8.22) * mm, "end": v(29.66, -7.89) * mm});
            skArc(sketch, "E10.42.3", {"start": v(30.67, -8.22) * mm, "mid": v(31.14, -8.51) * mm, "end": v(31.6, -8.84) * mm});
            skArc(sketch, "E10.42.4", {"start": v(31.6, -8.84) * mm, "mid": v(31.53, -9.08) * mm, "end": v(31.46, -9.32) * mm});
            skArc(sketch, "E10.42.5", {"start": v(31.31, -9.8) * mm, "mid": v(31.39, -9.56) * mm, "end": v(31.46, -9.32) * mm});
            skArc(sketch, "E10.43.0", {"start": v(31.06, -6.6) * mm, "mid": v(31.61, -6.55) * mm, "end": v(32.16, -6.47) * mm});
            skLineSegment(sketch, "E10.43.1", {"start": v(30.02, -6.38) * mm, "end": v(31.06, -6.6) * mm});
            skLineSegment(sketch, "E10.43.2", {"start": v(31.36, -4.97) * mm, "end": v(30.32, -4.75) * mm});
            skArc(sketch, "E10.43.3", {"start": v(31.36, -4.97) * mm, "mid": v(31.86, -5.21) * mm, "end": v(32.35, -5.49) * mm});
            skArc(sketch, "E10.43.4", {"start": v(32.35, -5.49) * mm, "mid": v(32.3, -5.73) * mm, "end": v(32.26, -5.98) * mm});
            skArc(sketch, "E10.43.5", {"start": v(32.16, -6.47) * mm, "mid": v(32.21, -6.22) * mm, "end": v(32.26, -5.98) * mm});
            skArc(sketch, "E10.44.0", {"start": v(31.58, -3.32) * mm, "mid": v(32.12, -3.21) * mm, "end": v(32.66, -3.07) * mm});
            skLineSegment(sketch, "E10.44.1", {"start": v(30.52, -3.2) * mm, "end": v(31.58, -3.32) * mm});
            skLineSegment(sketch, "E10.44.2", {"start": v(31.7, -1.66) * mm, "end": v(30.65, -1.55) * mm});
            skArc(sketch, "E10.44.3", {"start": v(31.7, -1.66) * mm, "mid": v(32.23, -1.85) * mm, "end": v(32.74, -2.08) * mm});
            skArc(sketch, "E10.44.4", {"start": v(32.74, -2.08) * mm, "mid": v(32.73, -2.33) * mm, "end": v(32.7, -2.57) * mm});
            skArc(sketch, "E10.44.5", {"start": v(32.66, -3.07) * mm, "mid": v(32.69, -2.82) * mm, "end": v(32.7, -2.57) * mm});
            skArc(sketch, "E10.45.0", {"start": v(31.75, 0) * mm, "mid": v(32.28, 0.16) * mm, "end": v(32.8, 0.36) * mm});
            skLineSegment(sketch, "E10.45.1", {"start": v(30.7, 0) * mm, "end": v(31.75, 0) * mm});
            skLineSegment(sketch, "E10.45.2", {"start": v(31.7, 1.66) * mm, "end": v(30.65, 1.66) * mm});
            skArc(sketch, "E10.45.3", {"start": v(31.7, 1.66) * mm, "mid": v(32.25, 1.53) * mm, "end": v(32.78, 1.36) * mm});
            skArc(sketch, "E10.45.4", {"start": v(32.78, 1.36) * mm, "mid": v(32.79, 1.1) * mm, "end": v(32.8, 0.86) * mm});
            skArc(sketch, "E10.45.5", {"start": v(32.8, 0.36) * mm, "mid": v(32.8, 0.6) * mm, "end": v(32.8, 0.86) * mm});
            skArc(sketch, "E10.46.0", {"start": v(31.58, 3.32) * mm, "mid": v(32.1, 3.54) * mm, "end": v(32.59, 3.79) * mm});
            skLineSegment(sketch, "E10.46.1", {"start": v(30.52, 3.2) * mm, "end": v(31.58, 3.32) * mm});
            skLineSegment(sketch, "E10.46.2", {"start": v(31.36, 4.97) * mm, "end": v(30.3, 4.86) * mm});
            skArc(sketch, "E10.46.3", {"start": v(31.36, 4.97) * mm, "mid": v(31.91, 4.9) * mm, "end": v(32.46, 4.78) * mm});
            skArc(sketch, "E10.46.4", {"start": v(32.46, 4.78) * mm, "mid": v(32.5, 4.53) * mm, "end": v(32.53, 4.28) * mm});
            skArc(sketch, "E10.46.5", {"start": v(32.59, 3.79) * mm, "mid": v(32.56, 4.04) * mm, "end": v(32.53, 4.28) * mm});
            skArc(sketch, "E10.47.0", {"start": v(31.06, 6.6) * mm, "mid": v(31.55, 6.87) * mm, "end": v(32.01, 7.17) * mm});
            skLineSegment(sketch, "E10.47.1", {"start": v(30.02, 6.38) * mm, "end": v(31.06, 6.6) * mm});
            skLineSegment(sketch, "E10.47.2", {"start": v(30.67, 8.22) * mm, "end": v(29.63, 8) * mm});
            skArc(sketch, "E10.47.3", {"start": v(30.67, 8.22) * mm, "mid": v(31.23, 8.2) * mm, "end": v(31.78, 8.14) * mm});
            skArc(sketch, "E10.47.4", {"start": v(31.78, 8.14) * mm, "mid": v(31.84, 7.9) * mm, "end": v(31.9, 7.66) * mm});
            skArc(sketch, "E10.47.5", {"start": v(32.01, 7.17) * mm, "mid": v(31.96, 7.42) * mm, "end": v(31.9, 7.66) * mm});
            skArc(sketch, "E10.48.0", {"start": v(30.2, 9.81) * mm, "mid": v(30.65, 10.13) * mm, "end": v(31.09, 10.48) * mm});
            skLineSegment(sketch, "E10.48.1", {"start": v(29.19, 9.48) * mm, "end": v(30.2, 9.81) * mm});
            skLineSegment(sketch, "E10.48.2", {"start": v(29.64, 11.38) * mm, "end": v(28.63, 11.05) * mm});
            skArc(sketch, "E10.48.3", {"start": v(29.64, 11.38) * mm, "mid": v(30.2, 11.42) * mm, "end": v(30.76, 11.42) * mm});
            skArc(sketch, "E10.48.4", {"start": v(30.76, 11.42) * mm, "mid": v(30.84, 11.19) * mm, "end": v(30.93, 10.95) * mm});
            skArc(sketch, "E10.48.5", {"start": v(31.09, 10.48) * mm, "mid": v(31, 10.72) * mm, "end": v(30.93, 10.95) * mm});
            skArc(sketch, "E10.49.0", {"start": v(29, 12.91) * mm, "mid": v(29.43, 13.28) * mm, "end": v(29.82, 13.67) * mm});
            skLineSegment(sketch, "E10.49.1", {"start": v(28.04, 12.48) * mm, "end": v(29, 12.91) * mm});
            skLineSegment(sketch, "E10.49.2", {"start": v(28.29, 14.41) * mm, "end": v(27.32, 13.98) * mm});
            skArc(sketch, "E10.49.3", {"start": v(28.29, 14.41) * mm, "mid": v(28.84, 14.51) * mm, "end": v(29.4, 14.57) * mm});
            skArc(sketch, "E10.49.4", {"start": v(29.4, 14.57) * mm, "mid": v(29.5, 14.35) * mm, "end": v(29.61, 14.12) * mm});
            skArc(sketch, "E10.49.5", {"start": v(29.82, 13.67) * mm, "mid": v(29.72, 13.9) * mm, "end": v(29.61, 14.12) * mm});
            skArc(sketch, "E10.50.0", {"start": v(27.5, 15.88) * mm, "mid": v(27.88, 16.28) * mm, "end": v(28.23, 16.72) * mm});
            skLineSegment(sketch, "E10.50.1", {"start": v(26.58, 15.35) * mm, "end": v(27.5, 15.88) * mm});
            skLineSegment(sketch, "E10.50.2", {"start": v(26.63, 17.3) * mm, "end": v(25.7, 16.76) * mm});
            skArc(sketch, "E10.50.3", {"start": v(26.63, 17.3) * mm, "mid": v(27.16, 17.45) * mm, "end": v(27.7, 17.56) * mm});
            skArc(sketch, "E10.50.4", {"start": v(27.7, 17.56) * mm, "mid": v(27.84, 17.35) * mm, "end": v(27.97, 17.14) * mm});
            skArc(sketch, "E10.50.5", {"start": v(28.23, 16.72) * mm, "mid": v(28.1, 16.93) * mm, "end": v(27.97, 17.14) * mm});
            skArc(sketch, "E10.51.0", {"start": v(25.69, 18.66) * mm, "mid": v(26.02, 19.1) * mm, "end": v(26.33, 19.57) * mm});
            skLineSegment(sketch, "E10.51.1", {"start": v(24.83, 18.04) * mm, "end": v(25.69, 18.66) * mm});
            skLineSegment(sketch, "E10.51.2", {"start": v(24.67, 19.98) * mm, "end": v(23.82, 19.36) * mm});
            skArc(sketch, "E10.51.3", {"start": v(24.67, 19.98) * mm, "mid": v(25.2, 20.2) * mm, "end": v(25.72, 20.36) * mm});
            skArc(sketch, "E10.51.4", {"start": v(25.72, 20.36) * mm, "mid": v(25.88, 20.17) * mm, "end": v(26.03, 19.97) * mm});
            skArc(sketch, "E10.51.5", {"start": v(26.33, 19.57) * mm, "mid": v(26.18, 19.77) * mm, "end": v(26.03, 19.97) * mm});
            skArc(sketch, "E10.52.0", {"start": v(23.6, 21.24) * mm, "mid": v(23.88, 21.72) * mm, "end": v(24.14, 22.22) * mm});
            skLineSegment(sketch, "E10.52.1", {"start": v(22.8, 20.54) * mm, "end": v(23.6, 21.24) * mm});
            skLineSegment(sketch, "E10.52.2", {"start": v(22.45, 22.45) * mm, "end": v(21.66, 21.74) * mm});
            skArc(sketch, "E10.52.3", {"start": v(22.45, 22.45) * mm, "mid": v(22.94, 22.71) * mm, "end": v(23.45, 22.94) * mm});
            skArc(sketch, "E10.52.4", {"start": v(23.45, 22.94) * mm, "mid": v(23.63, 22.76) * mm, "end": v(23.8, 22.58) * mm});
            skArc(sketch, "E10.52.5", {"start": v(24.14, 22.22) * mm, "mid": v(23.97, 22.4) * mm, "end": v(23.8, 22.58) * mm});
            skArc(sketch, "E10.53.0", {"start": v(21.24, 23.6) * mm, "mid": v(21.48, 24.1) * mm, "end": v(21.68, 24.62) * mm});
            skLineSegment(sketch, "E10.53.1", {"start": v(20.54, 22.8) * mm, "end": v(21.24, 23.6) * mm});
            skLineSegment(sketch, "E10.53.2", {"start": v(19.98, 24.67) * mm, "end": v(19.27, 23.89) * mm});
            skArc(sketch, "E10.53.3", {"start": v(19.98, 24.67) * mm, "mid": v(20.44, 24.99) * mm, "end": v(20.93, 25.27) * mm});
            skArc(sketch, "E10.53.4", {"start": v(20.93, 25.27) * mm, "mid": v(21.12, 25.1) * mm, "end": v(21.3, 24.95) * mm});
            skArc(sketch, "E10.53.5", {"start": v(21.68, 24.62) * mm, "mid": v(21.5, 24.78) * mm, "end": v(21.3, 24.95) * mm});
            skArc(sketch, "E10.54.0", {"start": v(18.66, 25.69) * mm, "mid": v(18.85, 26.21) * mm, "end": v(19, 26.75) * mm});
            skLineSegment(sketch, "E10.54.1", {"start": v(18.04, 24.83) * mm, "end": v(18.66, 25.69) * mm});
            skLineSegment(sketch, "E10.54.2", {"start": v(17.3, 26.63) * mm, "end": v(16.67, 25.77) * mm});
            skArc(sketch, "E10.54.3", {"start": v(17.3, 26.63) * mm, "mid": v(17.72, 26.99) * mm, "end": v(18.17, 27.32) * mm});
            skArc(sketch, "E10.54.4", {"start": v(18.17, 27.32) * mm, "mid": v(18.38, 27.18) * mm, "end": v(18.58, 27.04) * mm});
            skArc(sketch, "E10.54.5", {"start": v(19, 26.75) * mm, "mid": v(18.79, 26.9) * mm, "end": v(18.58, 27.04) * mm});
            skArc(sketch, "E10.55.0", {"start": v(15.87, 27.5) * mm, "mid": v(16, 28.04) * mm, "end": v(16.1, 28.6) * mm});
            skLineSegment(sketch, "E10.55.1", {"start": v(15.35, 26.58) * mm, "end": v(15.87, 27.5) * mm});
            skLineSegment(sketch, "E10.55.2", {"start": v(14.41, 28.29) * mm, "end": v(13.88, 27.37) * mm});
            skArc(sketch, "E10.55.3", {"start": v(14.41, 28.29) * mm, "mid": v(14.8, 28.7) * mm, "end": v(15.22, 29.07) * mm});
            skArc(sketch, "E10.55.4", {"start": v(15.22, 29.07) * mm, "mid": v(15.44, 28.95) * mm, "end": v(15.65, 28.83) * mm});
            skArc(sketch, "E10.55.5", {"start": v(16.1, 28.6) * mm, "mid": v(15.87, 28.71) * mm, "end": v(15.65, 28.83) * mm});
            skArc(sketch, "E10.56.0", {"start": v(12.91, 29) * mm, "mid": v(12.98, 29.56) * mm, "end": v(13.01, 30.12) * mm});
            skLineSegment(sketch, "E10.56.1", {"start": v(12.48, 28.04) * mm, "end": v(12.91, 29) * mm});
            skLineSegment(sketch, "E10.56.2", {"start": v(11.38, 29.64) * mm, "end": v(10.95, 28.67) * mm});
            skArc(sketch, "E10.56.3", {"start": v(11.38, 29.64) * mm, "mid": v(11.72, 30.08) * mm, "end": v(12.1, 30.5) * mm});
            skArc(sketch, "E10.56.4", {"start": v(12.1, 30.5) * mm, "mid": v(12.32, 30.4) * mm, "end": v(12.56, 30.31) * mm});
            skArc(sketch, "E10.56.5", {"start": v(13.01, 30.12) * mm, "mid": v(12.78, 30.21) * mm, "end": v(12.56, 30.31) * mm});
            skArc(sketch, "E10.57.0", {"start": v(9.81, 30.2) * mm, "mid": v(9.82, 30.75) * mm, "end": v(9.8, 31.31) * mm});
            skLineSegment(sketch, "E10.57.1", {"start": v(9.48, 29.19) * mm, "end": v(9.81, 30.2) * mm});
            skLineSegment(sketch, "E10.57.2", {"start": v(8.22, 30.67) * mm, "end": v(7.89, 29.66) * mm});
            skArc(sketch, "E10.57.3", {"start": v(8.22, 30.67) * mm, "mid": v(8.51, 31.14) * mm, "end": v(8.84, 31.6) * mm});
            skArc(sketch, "E10.57.4", {"start": v(8.84, 31.6) * mm, "mid": v(9.08, 31.53) * mm, "end": v(9.32, 31.46) * mm});
            skArc(sketch, "E10.57.5", {"start": v(9.8, 31.31) * mm, "mid": v(9.56, 31.39) * mm, "end": v(9.32, 31.46) * mm});
            skArc(sketch, "E10.58.0", {"start": v(6.6, 31.06) * mm, "mid": v(6.55, 31.61) * mm, "end": v(6.47, 32.16) * mm});
            skLineSegment(sketch, "E10.58.1", {"start": v(6.38, 30.02) * mm, "end": v(6.6, 31.06) * mm});
            skLineSegment(sketch, "E10.58.2", {"start": v(4.97, 31.36) * mm, "end": v(4.75, 30.32) * mm});
            skArc(sketch, "E10.58.3", {"start": v(4.97, 31.36) * mm, "mid": v(5.21, 31.86) * mm, "end": v(5.49, 32.35) * mm});
            skArc(sketch, "E10.58.4", {"start": v(5.49, 32.35) * mm, "mid": v(5.73, 32.3) * mm, "end": v(5.98, 32.26) * mm});
            skArc(sketch, "E10.58.5", {"start": v(6.47, 32.16) * mm, "mid": v(6.22, 32.21) * mm, "end": v(5.98, 32.26) * mm});
            skArc(sketch, "E10.59.0", {"start": v(3.32, 31.58) * mm, "mid": v(3.21, 32.12) * mm, "end": v(3.07, 32.66) * mm});
            skLineSegment(sketch, "E10.59.1", {"start": v(3.2, 30.52) * mm, "end": v(3.32, 31.58) * mm});
            skLineSegment(sketch, "E10.59.2", {"start": v(1.66, 31.7) * mm, "end": v(1.55, 30.65) * mm});
            skArc(sketch, "E10.59.3", {"start": v(1.66, 31.7) * mm, "mid": v(1.85, 32.23) * mm, "end": v(2.08, 32.74) * mm});
            skArc(sketch, "E10.59.4", {"start": v(2.08, 32.74) * mm, "mid": v(2.33, 32.73) * mm, "end": v(2.57, 32.7) * mm});
            skArc(sketch, "E10.59.5", {"start": v(3.07, 32.66) * mm, "mid": v(2.82, 32.69) * mm, "end": v(2.57, 32.7) * mm});
            skSolve(sketch);
        }
        {
            var Q0;
            Q0 = qSketchRegion(id + "F0", true);
            extrude(context, id + "F1", {"entities" : qUnion([Q0]), "depth" : 6.35 * mm});
        }
        {
            var Q0;
            Q0=makeQuery(id+"F1.opExtrude","CAP_FACE",FACE,{"disambiguationData":[OSD([sQuery(id+"F0.wireOp",EDGE,"E0"),sQuery(id+"F0.wireOp",EDGE,"E1"),sQuery(id+"F0.wireOp",EDGE,"E2"),sQuery(id+"F0.wireOp",EDGE,"E4.trimOffspring"),sQuery(id+"F0.wireOp",EDGE,"E5.trimOffspring"),sQuery(id+"F0.wireOp",EDGE,"E6.trimOffspring"),sQuery(id+"F0.wireOp",EDGE,"E7.MirrorCS"),sQuery(id+"F0.wireOp",EDGE,"E8.MirrorCS"),sQuery(id+"F0.wireOp",EDGE,"E9"),sQuery(id+"F0.wireOp",EDGE,"E10.1.0"),sQuery(id+"F0.wireOp",EDGE,"E10.1.1"),sQuery(id+"F0.wireOp",EDGE,"E10.1.2"),sQuery(id+"F0.wireOp",EDGE,"E10.1.3"),sQuery(id+"F0.wireOp",EDGE,"E10.1.4"),sQuery(id+"F0.wireOp",EDGE,"E10.1.5"),sQuery(id+"F0.wireOp",EDGE,"E10.2.0"),sQuery(id+"F0.wireOp",EDGE,"E10.2.1"),sQuery(id+"F0.wireOp",EDGE,"E10.2.2"),sQuery(id+"F0.wireOp",EDGE,"E10.2.3"),sQuery(id+"F0.wireOp",EDGE,"E10.2.4"),sQuery(id+"F0.wireOp",EDGE,"E10.2.5"),sQuery(id+"F0.wireOp",EDGE,"E10.3.0"),sQuery(id+"F0.wireOp",EDGE,"E10.3.1"),sQuery(id+"F0.wireOp",EDGE,"E10.3.2"),sQuery(id+"F0.wireOp",EDGE,"E10.3.3"),sQuery(id+"F0.wireOp",EDGE,"E10.3.4"),sQuery(id+"F0.wireOp",EDGE,"E10.3.5"),sQuery(id+"F0.wireOp",EDGE,"E10.4.0"),sQuery(id+"F0.wireOp",EDGE,"E10.4.1"),sQuery(id+"F0.wireOp",EDGE,"E10.4.2"),sQuery(id+"F0.wireOp",EDGE,"E10.4.3"),sQuery(id+"F0.wireOp",EDGE,"E10.4.4"),sQuery(id+"F0.wireOp",EDGE,"E10.4.5"),sQuery(id+"F0.wireOp",EDGE,"E10.5.0"),sQuery(id+"F0.wireOp",EDGE,"E10.5.1"),sQuery(id+"F0.wireOp",EDGE,"E10.5.2"),sQuery(id+"F0.wireOp",EDGE,"E10.5.3"),sQuery(id+"F0.wireOp",EDGE,"E10.5.4"),sQuery(id+"F0.wireOp",EDGE,"E10.5.5"),sQuery(id+"F0.wireOp",EDGE,"E10.6.0"),sQuery(id+"F0.wireOp",EDGE,"E10.6.1"),sQuery(id+"F0.wireOp",EDGE,"E10.6.2"),sQuery(id+"F0.wireOp",EDGE,"E10.6.3"),sQuery(id+"F0.wireOp",EDGE,"E10.6.4"),sQuery(id+"F0.wireOp",EDGE,"E10.6.5"),sQuery(id+"F0.wireOp",EDGE,"E10.7.0"),sQuery(id+"F0.wireOp",EDGE,"E10.7.1"),sQuery(id+"F0.wireOp",EDGE,"E10.7.2"),sQuery(id+"F0.wireOp",EDGE,"E10.7.3"),sQuery(id+"F0.wireOp",EDGE,"E10.7.4"),sQuery(id+"F0.wireOp",EDGE,"E10.7.5"),sQuery(id+"F0.wireOp",EDGE,"E10.8.0"),sQuery(id+"F0.wireOp",EDGE,"E10.8.1"),sQuery(id+"F0.wireOp",EDGE,"E10.8.2"),sQuery(id+"F0.wireOp",EDGE,"E10.8.3"),sQuery(id+"F0.wireOp",EDGE,"E10.8.4"),sQuery(id+"F0.wireOp",EDGE,"E10.8.5"),sQuery(id+"F0.wireOp",EDGE,"E10.9.0"),sQuery(id+"F0.wireOp",EDGE,"E10.9.1"),sQuery(id+"F0.wireOp",EDGE,"E10.9.2"),sQuery(id+"F0.wireOp",EDGE,"E10.9.3"),sQuery(id+"F0.wireOp",EDGE,"E10.9.4"),sQuery(id+"F0.wireOp",EDGE,"E10.9.5"),sQuery(id+"F0.wireOp",EDGE,"E10.10.0"),sQuery(id+"F0.wireOp",EDGE,"E10.10.1"),sQuery(id+"F0.wireOp",EDGE,"E10.10.2"),sQuery(id+"F0.wireOp",EDGE,"E10.10.3"),sQuery(id+"F0.wireOp",EDGE,"E10.10.4"),sQuery(id+"F0.wireOp",EDGE,"E10.10.5"),sQuery(id+"F0.wireOp",EDGE,"E10.11.0"),sQuery(id+"F0.wireOp",EDGE,"E10.11.1"),sQuery(id+"F0.wireOp",EDGE,"E10.11.2"),sQuery(id+"F0.wireOp",EDGE,"E10.11.3"),sQuery(id+"F0.wireOp",EDGE,"E10.11.4"),sQuery(id+"F0.wireOp",EDGE,"E10.11.5"),sQuery(id+"F0.wireOp",EDGE,"E10.12.0"),sQuery(id+"F0.wireOp",EDGE,"E10.12.1"),sQuery(id+"F0.wireOp",EDGE,"E10.12.2"),sQuery(id+"F0.wireOp",EDGE,"E10.12.3"),sQuery(id+"F0.wireOp",EDGE,"E10.12.4"),sQuery(id+"F0.wireOp",EDGE,"E10.12.5"),sQuery(id+"F0.wireOp",EDGE,"E10.13.0"),sQuery(id+"F0.wireOp",EDGE,"E10.13.1"),sQuery(id+"F0.wireOp",EDGE,"E10.13.2"),sQuery(id+"F0.wireOp",EDGE,"E10.13.3"),sQuery(id+"F0.wireOp",EDGE,"E10.13.4"),sQuery(id+"F0.wireOp",EDGE,"E10.13.5"),sQuery(id+"F0.wireOp",EDGE,"E10.14.0"),sQuery(id+"F0.wireOp",EDGE,"E10.14.1"),sQuery(id+"F0.wireOp",EDGE,"E10.14.2"),sQuery(id+"F0.wireOp",EDGE,"E10.14.3"),sQuery(id+"F0.wireOp",EDGE,"E10.14.4"),sQuery(id+"F0.wireOp",EDGE,"E10.14.5"),sQuery(id+"F0.wireOp",EDGE,"E10.15.0"),sQuery(id+"F0.wireOp",EDGE,"E10.15.1"),sQuery(id+"F0.wireOp",EDGE,"E10.15.2"),sQuery(id+"F0.wireOp",EDGE,"E10.15.3"),sQuery(id+"F0.wireOp",EDGE,"E10.15.4"),sQuery(id+"F0.wireOp",EDGE,"E10.15.5"),sQuery(id+"F0.wireOp",EDGE,"E10.16.0"),sQuery(id+"F0.wireOp",EDGE,"E10.16.1"),sQuery(id+"F0.wireOp",EDGE,"E10.16.2"),sQuery(id+"F0.wireOp",EDGE,"E10.16.3"),sQuery(id+"F0.wireOp",EDGE,"E10.16.4"),sQuery(id+"F0.wireOp",EDGE,"E10.16.5"),sQuery(id+"F0.wireOp",EDGE,"E10.17.0"),sQuery(id+"F0.wireOp",EDGE,"E10.17.1"),sQuery(id+"F0.wireOp",EDGE,"E10.17.2"),sQuery(id+"F0.wireOp",EDGE,"E10.17.3"),sQuery(id+"F0.wireOp",EDGE,"E10.17.4"),sQuery(id+"F0.wireOp",EDGE,"E10.17.5"),sQuery(id+"F0.wireOp",EDGE,"E10.18.0"),sQuery(id+"F0.wireOp",EDGE,"E10.18.1"),sQuery(id+"F0.wireOp",EDGE,"E10.18.2"),sQuery(id+"F0.wireOp",EDGE,"E10.18.3"),sQuery(id+"F0.wireOp",EDGE,"E10.18.4"),sQuery(id+"F0.wireOp",EDGE,"E10.18.5"),sQuery(id+"F0.wireOp",EDGE,"E10.19.0"),sQuery(id+"F0.wireOp",EDGE,"E10.19.1"),sQuery(id+"F0.wireOp",EDGE,"E10.19.2"),sQuery(id+"F0.wireOp",EDGE,"E10.19.3"),sQuery(id+"F0.wireOp",EDGE,"E10.19.4"),sQuery(id+"F0.wireOp",EDGE,"E10.19.5"),sQuery(id+"F0.wireOp",EDGE,"E10.20.0"),sQuery(id+"F0.wireOp",EDGE,"E10.20.1"),sQuery(id+"F0.wireOp",EDGE,"E10.20.2"),sQuery(id+"F0.wireOp",EDGE,"E10.20.3"),sQuery(id+"F0.wireOp",EDGE,"E10.20.4"),sQuery(id+"F0.wireOp",EDGE,"E10.20.5"),sQuery(id+"F0.wireOp",EDGE,"E10.21.0"),sQuery(id+"F0.wireOp",EDGE,"E10.21.1"),sQuery(id+"F0.wireOp",EDGE,"E10.21.2"),sQuery(id+"F0.wireOp",EDGE,"E10.21.3"),sQuery(id+"F0.wireOp",EDGE,"E10.21.4"),sQuery(id+"F0.wireOp",EDGE,"E10.21.5"),sQuery(id+"F0.wireOp",EDGE,"E10.22.0"),sQuery(id+"F0.wireOp",EDGE,"E10.22.1"),sQuery(id+"F0.wireOp",EDGE,"E10.22.2"),sQuery(id+"F0.wireOp",EDGE,"E10.22.3"),sQuery(id+"F0.wireOp",EDGE,"E10.22.4"),sQuery(id+"F0.wireOp",EDGE,"E10.22.5"),sQuery(id+"F0.wireOp",EDGE,"E10.23.0"),sQuery(id+"F0.wireOp",EDGE,"E10.23.1"),sQuery(id+"F0.wireOp",EDGE,"E10.23.2"),sQuery(id+"F0.wireOp",EDGE,"E10.23.3"),sQuery(id+"F0.wireOp",EDGE,"E10.23.4"),sQuery(id+"F0.wireOp",EDGE,"E10.23.5"),sQuery(id+"F0.wireOp",EDGE,"E10.24.0"),sQuery(id+"F0.wireOp",EDGE,"E10.24.1"),sQuery(id+"F0.wireOp",EDGE,"E10.24.2"),sQuery(id+"F0.wireOp",EDGE,"E10.24.3"),sQuery(id+"F0.wireOp",EDGE,"E10.24.4"),sQuery(id+"F0.wireOp",EDGE,"E10.24.5"),sQuery(id+"F0.wireOp",EDGE,"E10.25.0"),sQuery(id+"F0.wireOp",EDGE,"E10.25.1"),sQuery(id+"F0.wireOp",EDGE,"E10.25.2"),sQuery(id+"F0.wireOp",EDGE,"E10.25.3"),sQuery(id+"F0.wireOp",EDGE,"E10.25.4"),sQuery(id+"F0.wireOp",EDGE,"E10.25.5"),sQuery(id+"F0.wireOp",EDGE,"E10.26.0"),sQuery(id+"F0.wireOp",EDGE,"E10.26.1"),sQuery(id+"F0.wireOp",EDGE,"E10.26.2"),sQuery(id+"F0.wireOp",EDGE,"E10.26.3"),sQuery(id+"F0.wireOp",EDGE,"E10.26.4"),sQuery(id+"F0.wireOp",EDGE,"E10.26.5"),sQuery(id+"F0.wireOp",EDGE,"E10.27.0"),sQuery(id+"F0.wireOp",EDGE,"E10.27.1"),sQuery(id+"F0.wireOp",EDGE,"E10.27.2"),sQuery(id+"F0.wireOp",EDGE,"E10.27.3"),sQuery(id+"F0.wireOp",EDGE,"E10.27.4"),sQuery(id+"F0.wireOp",EDGE,"E10.27.5"),sQuery(id+"F0.wireOp",EDGE,"E10.28.0"),sQuery(id+"F0.wireOp",EDGE,"E10.28.1"),sQuery(id+"F0.wireOp",EDGE,"E10.28.2"),sQuery(id+"F0.wireOp",EDGE,"E10.28.3"),sQuery(id+"F0.wireOp",EDGE,"E10.28.4"),sQuery(id+"F0.wireOp",EDGE,"E10.28.5"),sQuery(id+"F0.wireOp",EDGE,"E10.29.0"),sQuery(id+"F0.wireOp",EDGE,"E10.29.1"),sQuery(id+"F0.wireOp",EDGE,"E10.29.2"),sQuery(id+"F0.wireOp",EDGE,"E10.29.3"),sQuery(id+"F0.wireOp",EDGE,"E10.29.4"),sQuery(id+"F0.wireOp",EDGE,"E10.29.5"),sQuery(id+"F0.wireOp",EDGE,"E10.30.0"),sQuery(id+"F0.wireOp",EDGE,"E10.30.1"),sQuery(id+"F0.wireOp",EDGE,"E10.30.2"),sQuery(id+"F0.wireOp",EDGE,"E10.30.3"),sQuery(id+"F0.wireOp",EDGE,"E10.30.4"),sQuery(id+"F0.wireOp",EDGE,"E10.30.5"),sQuery(id+"F0.wireOp",EDGE,"E10.31.0"),sQuery(id+"F0.wireOp",EDGE,"E10.31.1"),sQuery(id+"F0.wireOp",EDGE,"E10.31.2"),sQuery(id+"F0.wireOp",EDGE,"E10.31.3"),sQuery(id+"F0.wireOp",EDGE,"E10.31.4"),sQuery(id+"F0.wireOp",EDGE,"E10.31.5"),sQuery(id+"F0.wireOp",EDGE,"E10.32.0"),sQuery(id+"F0.wireOp",EDGE,"E10.32.1"),sQuery(id+"F0.wireOp",EDGE,"E10.32.2"),sQuery(id+"F0.wireOp",EDGE,"E10.32.3"),sQuery(id+"F0.wireOp",EDGE,"E10.32.4"),sQuery(id+"F0.wireOp",EDGE,"E10.32.5"),sQuery(id+"F0.wireOp",EDGE,"E10.33.0"),sQuery(id+"F0.wireOp",EDGE,"E10.33.1"),sQuery(id+"F0.wireOp",EDGE,"E10.33.2"),sQuery(id+"F0.wireOp",EDGE,"E10.33.3"),sQuery(id+"F0.wireOp",EDGE,"E10.33.4"),sQuery(id+"F0.wireOp",EDGE,"E10.33.5"),sQuery(id+"F0.wireOp",EDGE,"E10.34.0"),sQuery(id+"F0.wireOp",EDGE,"E10.34.1"),sQuery(id+"F0.wireOp",EDGE,"E10.34.2"),sQuery(id+"F0.wireOp",EDGE,"E10.34.3"),sQuery(id+"F0.wireOp",EDGE,"E10.34.4"),sQuery(id+"F0.wireOp",EDGE,"E10.34.5"),sQuery(id+"F0.wireOp",EDGE,"E10.35.0"),sQuery(id+"F0.wireOp",EDGE,"E10.35.1"),sQuery(id+"F0.wireOp",EDGE,"E10.35.2"),sQuery(id+"F0.wireOp",EDGE,"E10.35.3"),sQuery(id+"F0.wireOp",EDGE,"E10.35.4"),sQuery(id+"F0.wireOp",EDGE,"E10.35.5"),sQuery(id+"F0.wireOp",EDGE,"E10.36.0"),sQuery(id+"F0.wireOp",EDGE,"E10.36.1"),sQuery(id+"F0.wireOp",EDGE,"E10.36.2"),sQuery(id+"F0.wireOp",EDGE,"E10.36.3"),sQuery(id+"F0.wireOp",EDGE,"E10.36.4"),sQuery(id+"F0.wireOp",EDGE,"E10.36.5"),sQuery(id+"F0.wireOp",EDGE,"E10.37.0"),sQuery(id+"F0.wireOp",EDGE,"E10.37.1"),sQuery(id+"F0.wireOp",EDGE,"E10.37.2"),sQuery(id+"F0.wireOp",EDGE,"E10.37.3"),sQuery(id+"F0.wireOp",EDGE,"E10.37.4"),sQuery(id+"F0.wireOp",EDGE,"E10.37.5"),sQuery(id+"F0.wireOp",EDGE,"E10.38.0"),sQuery(id+"F0.wireOp",EDGE,"E10.38.1"),sQuery(id+"F0.wireOp",EDGE,"E10.38.2"),sQuery(id+"F0.wireOp",EDGE,"E10.38.3"),sQuery(id+"F0.wireOp",EDGE,"E10.38.4"),sQuery(id+"F0.wireOp",EDGE,"E10.38.5"),sQuery(id+"F0.wireOp",EDGE,"E10.39.0"),sQuery(id+"F0.wireOp",EDGE,"E10.39.1"),sQuery(id+"F0.wireOp",EDGE,"E10.39.2"),sQuery(id+"F0.wireOp",EDGE,"E10.39.3"),sQuery(id+"F0.wireOp",EDGE,"E10.39.4"),sQuery(id+"F0.wireOp",EDGE,"E10.39.5"),sQuery(id+"F0.wireOp",EDGE,"E10.40.0"),sQuery(id+"F0.wireOp",EDGE,"E10.40.1"),sQuery(id+"F0.wireOp",EDGE,"E10.40.2"),sQuery(id+"F0.wireOp",EDGE,"E10.40.3"),sQuery(id+"F0.wireOp",EDGE,"E10.40.4"),sQuery(id+"F0.wireOp",EDGE,"E10.40.5"),sQuery(id+"F0.wireOp",EDGE,"E10.41.0"),sQuery(id+"F0.wireOp",EDGE,"E10.41.1"),sQuery(id+"F0.wireOp",EDGE,"E10.41.2"),sQuery(id+"F0.wireOp",EDGE,"E10.41.3"),sQuery(id+"F0.wireOp",EDGE,"E10.41.4"),sQuery(id+"F0.wireOp",EDGE,"E10.41.5"),sQuery(id+"F0.wireOp",EDGE,"E10.42.0"),sQuery(id+"F0.wireOp",EDGE,"E10.42.1"),sQuery(id+"F0.wireOp",EDGE,"E10.42.2"),sQuery(id+"F0.wireOp",EDGE,"E10.42.3"),sQuery(id+"F0.wireOp",EDGE,"E10.42.4"),sQuery(id+"F0.wireOp",EDGE,"E10.42.5"),sQuery(id+"F0.wireOp",EDGE,"E10.43.0"),sQuery(id+"F0.wireOp",EDGE,"E10.43.1"),sQuery(id+"F0.wireOp",EDGE,"E10.43.2"),sQuery(id+"F0.wireOp",EDGE,"E10.43.3"),sQuery(id+"F0.wireOp",EDGE,"E10.43.4"),sQuery(id+"F0.wireOp",EDGE,"E10.43.5"),sQuery(id+"F0.wireOp",EDGE,"E10.44.0"),sQuery(id+"F0.wireOp",EDGE,"E10.44.1"),sQuery(id+"F0.wireOp",EDGE,"E10.44.2"),sQuery(id+"F0.wireOp",EDGE,"E10.44.3"),sQuery(id+"F0.wireOp",EDGE,"E10.44.4"),sQuery(id+"F0.wireOp",EDGE,"E10.44.5"),sQuery(id+"F0.wireOp",EDGE,"E10.45.0"),sQuery(id+"F0.wireOp",EDGE,"E10.45.1"),sQuery(id+"F0.wireOp",EDGE,"E10.45.2"),sQuery(id+"F0.wireOp",EDGE,"E10.45.3"),sQuery(id+"F0.wireOp",EDGE,"E10.45.4"),sQuery(id+"F0.wireOp",EDGE,"E10.45.5"),sQuery(id+"F0.wireOp",EDGE,"E10.46.0"),sQuery(id+"F0.wireOp",EDGE,"E10.46.1"),sQuery(id+"F0.wireOp",EDGE,"E10.46.2"),sQuery(id+"F0.wireOp",EDGE,"E10.46.3"),sQuery(id+"F0.wireOp",EDGE,"E10.46.4"),sQuery(id+"F0.wireOp",EDGE,"E10.46.5"),sQuery(id+"F0.wireOp",EDGE,"E10.47.0"),sQuery(id+"F0.wireOp",EDGE,"E10.47.1"),sQuery(id+"F0.wireOp",EDGE,"E10.47.2"),sQuery(id+"F0.wireOp",EDGE,"E10.47.3"),sQuery(id+"F0.wireOp",EDGE,"E10.47.4"),sQuery(id+"F0.wireOp",EDGE,"E10.47.5"),sQuery(id+"F0.wireOp",EDGE,"E10.48.0"),sQuery(id+"F0.wireOp",EDGE,"E10.48.1"),sQuery(id+"F0.wireOp",EDGE,"E10.48.2"),sQuery(id+"F0.wireOp",EDGE,"E10.48.3"),sQuery(id+"F0.wireOp",EDGE,"E10.48.4"),sQuery(id+"F0.wireOp",EDGE,"E10.48.5"),sQuery(id+"F0.wireOp",EDGE,"E10.49.0"),sQuery(id+"F0.wireOp",EDGE,"E10.49.1"),sQuery(id+"F0.wireOp",EDGE,"E10.49.2"),sQuery(id+"F0.wireOp",EDGE,"E10.49.3"),sQuery(id+"F0.wireOp",EDGE,"E10.49.4"),sQuery(id+"F0.wireOp",EDGE,"E10.49.5"),sQuery(id+"F0.wireOp",EDGE,"E10.50.0"),sQuery(id+"F0.wireOp",EDGE,"E10.50.1"),sQuery(id+"F0.wireOp",EDGE,"E10.50.2"),sQuery(id+"F0.wireOp",EDGE,"E10.50.3"),sQuery(id+"F0.wireOp",EDGE,"E10.50.4"),sQuery(id+"F0.wireOp",EDGE,"E10.50.5"),sQuery(id+"F0.wireOp",EDGE,"E10.51.0"),sQuery(id+"F0.wireOp",EDGE,"E10.51.1"),sQuery(id+"F0.wireOp",EDGE,"E10.51.2"),sQuery(id+"F0.wireOp",EDGE,"E10.51.3"),sQuery(id+"F0.wireOp",EDGE,"E10.51.4"),sQuery(id+"F0.wireOp",EDGE,"E10.51.5"),sQuery(id+"F0.wireOp",EDGE,"E10.52.0"),sQuery(id+"F0.wireOp",EDGE,"E10.52.1"),sQuery(id+"F0.wireOp",EDGE,"E10.52.2"),sQuery(id+"F0.wireOp",EDGE,"E10.52.3"),sQuery(id+"F0.wireOp",EDGE,"E10.52.4"),sQuery(id+"F0.wireOp",EDGE,"E10.52.5"),sQuery(id+"F0.wireOp",EDGE,"E10.53.0"),sQuery(id+"F0.wireOp",EDGE,"E10.53.1"),sQuery(id+"F0.wireOp",EDGE,"E10.53.2"),sQuery(id+"F0.wireOp",EDGE,"E10.53.3"),sQuery(id+"F0.wireOp",EDGE,"E10.53.4"),sQuery(id+"F0.wireOp",EDGE,"E10.53.5"),sQuery(id+"F0.wireOp",EDGE,"E10.54.0"),sQuery(id+"F0.wireOp",EDGE,"E10.54.1"),sQuery(id+"F0.wireOp",EDGE,"E10.54.2"),sQuery(id+"F0.wireOp",EDGE,"E10.54.3"),sQuery(id+"F0.wireOp",EDGE,"E10.54.4"),sQuery(id+"F0.wireOp",EDGE,"E10.54.5"),sQuery(id+"F0.wireOp",EDGE,"E10.55.0"),sQuery(id+"F0.wireOp",EDGE,"E10.55.1"),sQuery(id+"F0.wireOp",EDGE,"E10.55.2"),sQuery(id+"F0.wireOp",EDGE,"E10.55.3"),sQuery(id+"F0.wireOp",EDGE,"E10.55.4"),sQuery(id+"F0.wireOp",EDGE,"E10.55.5"),sQuery(id+"F0.wireOp",EDGE,"E10.56.0"),sQuery(id+"F0.wireOp",EDGE,"E10.56.1"),sQuery(id+"F0.wireOp",EDGE,"E10.56.2"),sQuery(id+"F0.wireOp",EDGE,"E10.56.3"),sQuery(id+"F0.wireOp",EDGE,"E10.56.4"),sQuery(id+"F0.wireOp",EDGE,"E10.56.5"),sQuery(id+"F0.wireOp",EDGE,"E10.57.0"),sQuery(id+"F0.wireOp",EDGE,"E10.57.1"),sQuery(id+"F0.wireOp",EDGE,"E10.57.2"),sQuery(id+"F0.wireOp",EDGE,"E10.57.3"),sQuery(id+"F0.wireOp",EDGE,"E10.57.4"),sQuery(id+"F0.wireOp",EDGE,"E10.57.5"),sQuery(id+"F0.wireOp",EDGE,"E10.58.0"),sQuery(id+"F0.wireOp",EDGE,"E10.58.1"),sQuery(id+"F0.wireOp",EDGE,"E10.58.2"),sQuery(id+"F0.wireOp",EDGE,"E10.58.3"),sQuery(id+"F0.wireOp",EDGE,"E10.58.4"),sQuery(id+"F0.wireOp",EDGE,"E10.58.5"),sQuery(id+"F0.wireOp",EDGE,"E10.59.0"),sQuery(id+"F0.wireOp",EDGE,"E10.59.1"),sQuery(id+"F0.wireOp",EDGE,"E10.59.2"),sQuery(id+"F0.wireOp",EDGE,"E10.59.3"),sQuery(id+"F0.wireOp",EDGE,"E10.59.4"),sQuery(id+"F0.wireOp",EDGE,"E10.59.5")])],"isStart":false});
            var sketch = newSketch(context, id + "F2", { "sketchPlane" : qUnion([Q0])});
            skCircle(sketch, "E11", {"center": v(0, 0) * mm, "radius": 11.43 * mm});
            skSolve(sketch);
        }
        {
            var Q0;
            Q0=makeQuery(id+"F2.imprint","IMPRINT",FACE,{"disambiguationData":[TD([[makeQuery(id+"F2.imprint","IMPRINT",EDGE,{"derivedFrom":sQuery(id+"F2.wireOp",EDGE,"E11")}),1.0]])]});
            extrude(context, id + "F3", {"entities" : qUnion([Q0]), "operationType" : NewBodyOperationType.ADD, "depth" : 7.37 * mm});
        }
        {
            var Q0;
            Q0=makeQuery(id+"F3.opExtrude","CAP_FACE",FACE,{"disambiguationData":[OSD([sQuery(id+"F2.wireOp",EDGE,"E11")])],"isStart":false});
            var sketch = newSketch(context, id + "F4", { "sketchPlane" : qUnion([Q0])});
            skCircle(sketch, "E12.cCircle", {"center": v(0, 0) * mm, "radius": 5.56 * mm, "construction": true});
            skLineSegment(sketch, "E12.0", {"start": v(2.65, 4.89) * mm, "end": v(5.55, 0.15) * mm});
            skLineSegment(sketch, "E12.1", {"start": v(5.55, 0.15) * mm, "end": v(2.9, -4.73) * mm});
            skLineSegment(sketch, "E12.2", {"start": v(2.9, -4.73) * mm, "end": v(-2.65, -4.89) * mm});
            skLineSegment(sketch, "E12.3", {"start": v(-2.65, -4.89) * mm, "end": v(-5.55, -0.15) * mm});
            skLineSegment(sketch, "E12.4", {"start": v(-5.55, -0.15) * mm, "end": v(-2.9, 4.73) * mm});
            skLineSegment(sketch, "E12.5", {"start": v(-2.9, 4.73) * mm, "end": v(2.65, 4.89) * mm});
            skSolve(sketch);
        }
        {
            var Q0;
            Q0 = qSketchRegion(id + "F4", true);
            extrude(context, id + "F5", {"entities" : qUnion([Q0]), "operationType" : NewBodyOperationType.REMOVE, "oppositeDirection" : true, "depth" : 64 * mm});
        }
    });
